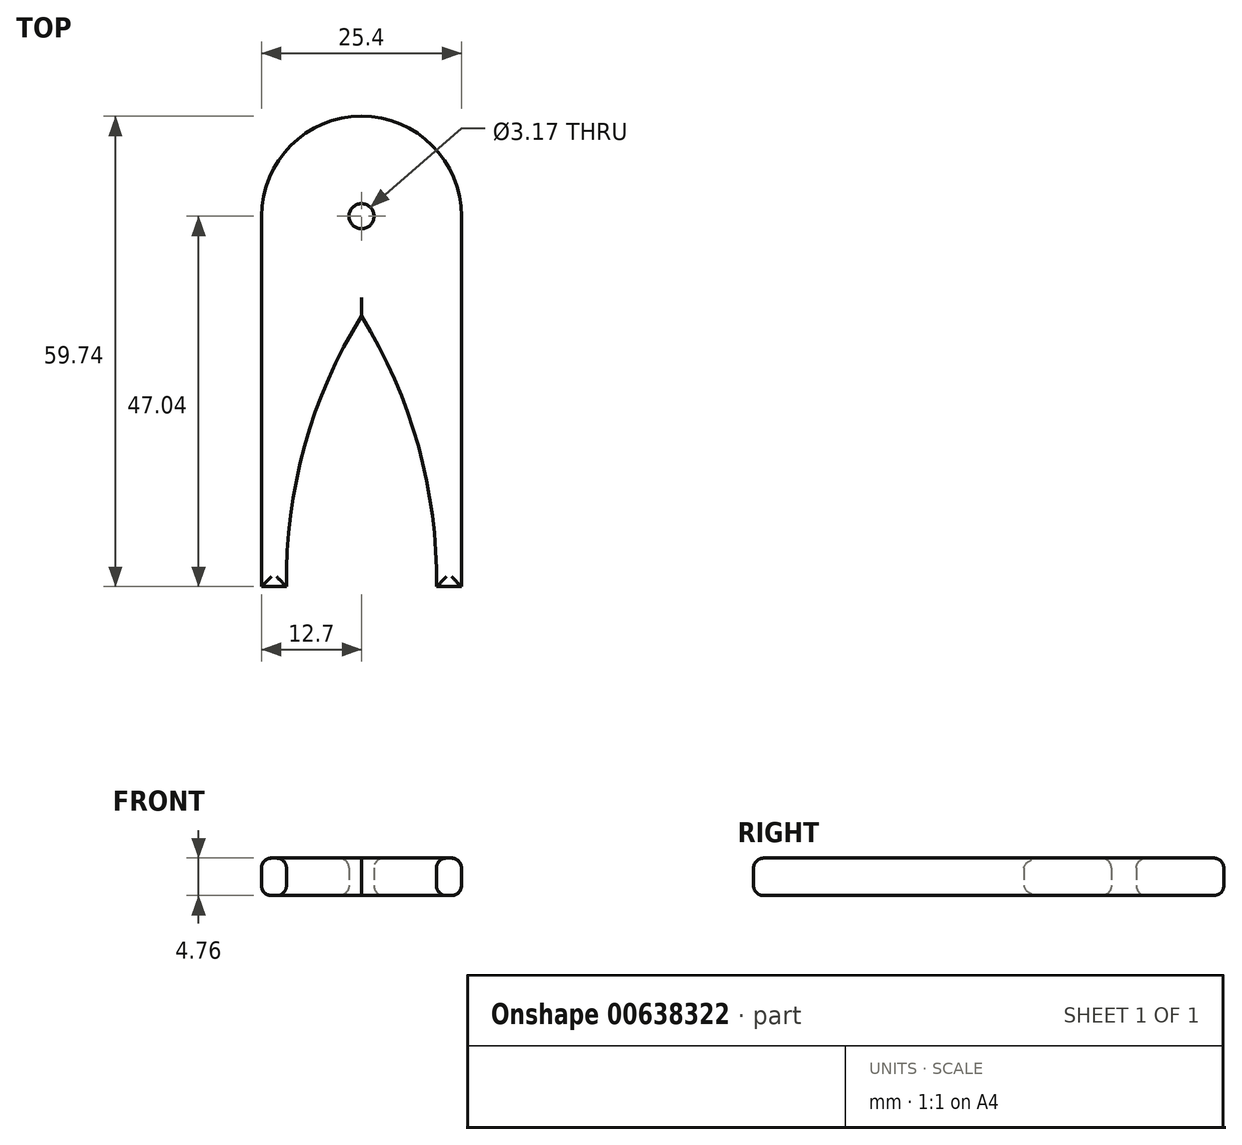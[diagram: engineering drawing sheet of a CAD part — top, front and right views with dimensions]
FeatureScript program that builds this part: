
annotation { "Feature Type Name" : "Feature", "Feature Type Description" : "" }
export const myFeature = defineFeature(function(context is Context, id is Id, definition is map)
    precondition{}
    {
        {
            var Q0;
            Q0=qCreatedBy(makeId("Top.planeOp"),FACE);
            var sketch = newSketch(context, id + "F0", { "sketchPlane" : qUnion([Q0])});
            skArc(sketch, "E0", {"start": v(0, 12.7) * mm, "mid": v(-8.98, 8.98) * mm, "end": v(-12.7, 0) * mm});
            skLineSegment(sketch, "E1", {"start": v(-12.7, 0) * mm, "end": v(-12.7, -47.04) * mm});
            skPoint(sketch, "E2.orphan", {"position": v(0, 12.7) * mm});
            skPoint(sketch, "E3.second.point", {"position": v(-13.78, -47.04) * mm});
            skLineSegment(sketch, "E4", {"start": v(0, -9.32) * mm, "end": v(0, -12.7) * mm});
            skPoint(sketch, "E5.orphan", {"position": v(12.7, 0) * mm});
            skArc(sketch, "E6.MirrorCS", {"start": v(0, 12.7) * mm, "mid": v(8.98, 8.98) * mm, "end": v(12.7, 0) * mm});
            skPoint(sketch, "E7.MirrorP", {"position": v(-12.7, 0) * mm});
            skLineSegment(sketch, "E8.MirrorCS", {"start": v(12.7, 0) * mm, "end": v(12.7, -47.04) * mm});
            skPoint(sketch, "E9.orphan", {"position": v(0, -12.7) * mm});
            skCircle(sketch, "E10", {"center": v(0, 0) * mm, "radius": 1.59 * mm});
            skLineSegment(sketch, "E11", {"start": v(-12.7, 0) * mm, "end": v(-12.7, 17.07) * mm, "construction": true});
            skLineSegment(sketch, "E12", {"start": v(12.7, 0) * mm, "end": v(12.7, 17.07) * mm, "construction": true});
            skLineSegment(sketch, "E13", {"start": v(-12.7, -47.04) * mm, "end": v(-9.52, -47.04) * mm});
            skArc(sketch, "E14", {"start": v(9.53, -47.04) * mm, "mid": v(7.22, -29.19) * mm, "end": v(0, -12.7) * mm});
            skArc(sketch, "E15", {"start": v(0, -12.7) * mm, "mid": v(-7.22, -29.19) * mm, "end": v(-9.52, -47.04) * mm});
            skLineSegment(sketch, "E16", {"start": v(9.53, -47.04) * mm, "end": v(12.7, -47.04) * mm});
            skSolve(sketch);
        }
        {
            var Q0;
            Q0=makeQuery(id+"F0.imprint","IMPRINT",FACE,{"disambiguationData":[TD([[makeQuery(id+"F0.imprint","IMPRINT",EDGE,{"derivedFrom":sQuery(id+"F0.wireOp",EDGE,"E0")}),1.0]])]});
            extrude(context, id + "F1", {"entities" : qUnion([Q0]), "depth" : 4.76 * mm, "offsetDistance" : 25.4 * mm});
        }
        {
            var Q0;
            Q0=makeQuery(id+"F1.opExtrude","CAP_FACE",FACE,{"disambiguationData":[OSD([sQuery(id+"F0.wireOp",EDGE,"E0"),sQuery(id+"F0.wireOp",EDGE,"E1"),sQuery(id+"F0.wireOp",EDGE,"E6.MirrorCS"),sQuery(id+"F0.wireOp",EDGE,"E8.MirrorCS"),sQuery(id+"F0.wireOp",EDGE,"E10"),sQuery(id+"F0.wireOp",EDGE,"E13"),sQuery(id+"F0.wireOp",EDGE,"E14"),sQuery(id+"F0.wireOp",EDGE,"E15"),sQuery(id+"F0.wireOp",EDGE,"E16")])],"isStart":true});
            var Q1;
            Q1=makeQuery(id+"F1.opExtrude","CAP_FACE",FACE,{"disambiguationData":[OSD([sQuery(id+"F0.wireOp",EDGE,"E0"),sQuery(id+"F0.wireOp",EDGE,"E1"),sQuery(id+"F0.wireOp",EDGE,"E6.MirrorCS"),sQuery(id+"F0.wireOp",EDGE,"E8.MirrorCS"),sQuery(id+"F0.wireOp",EDGE,"E10"),sQuery(id+"F0.wireOp",EDGE,"E13"),sQuery(id+"F0.wireOp",EDGE,"E14"),sQuery(id+"F0.wireOp",EDGE,"E15"),sQuery(id+"F0.wireOp",EDGE,"E16")])],"isStart":false});
            fillet(context, id + "F2", {"entities" : qUnion([Q0, Q1]), "radius" : 1.27 * mm, "tangentPropagation" : true, "allowEdgeOverflow" : false});
        }
    });
